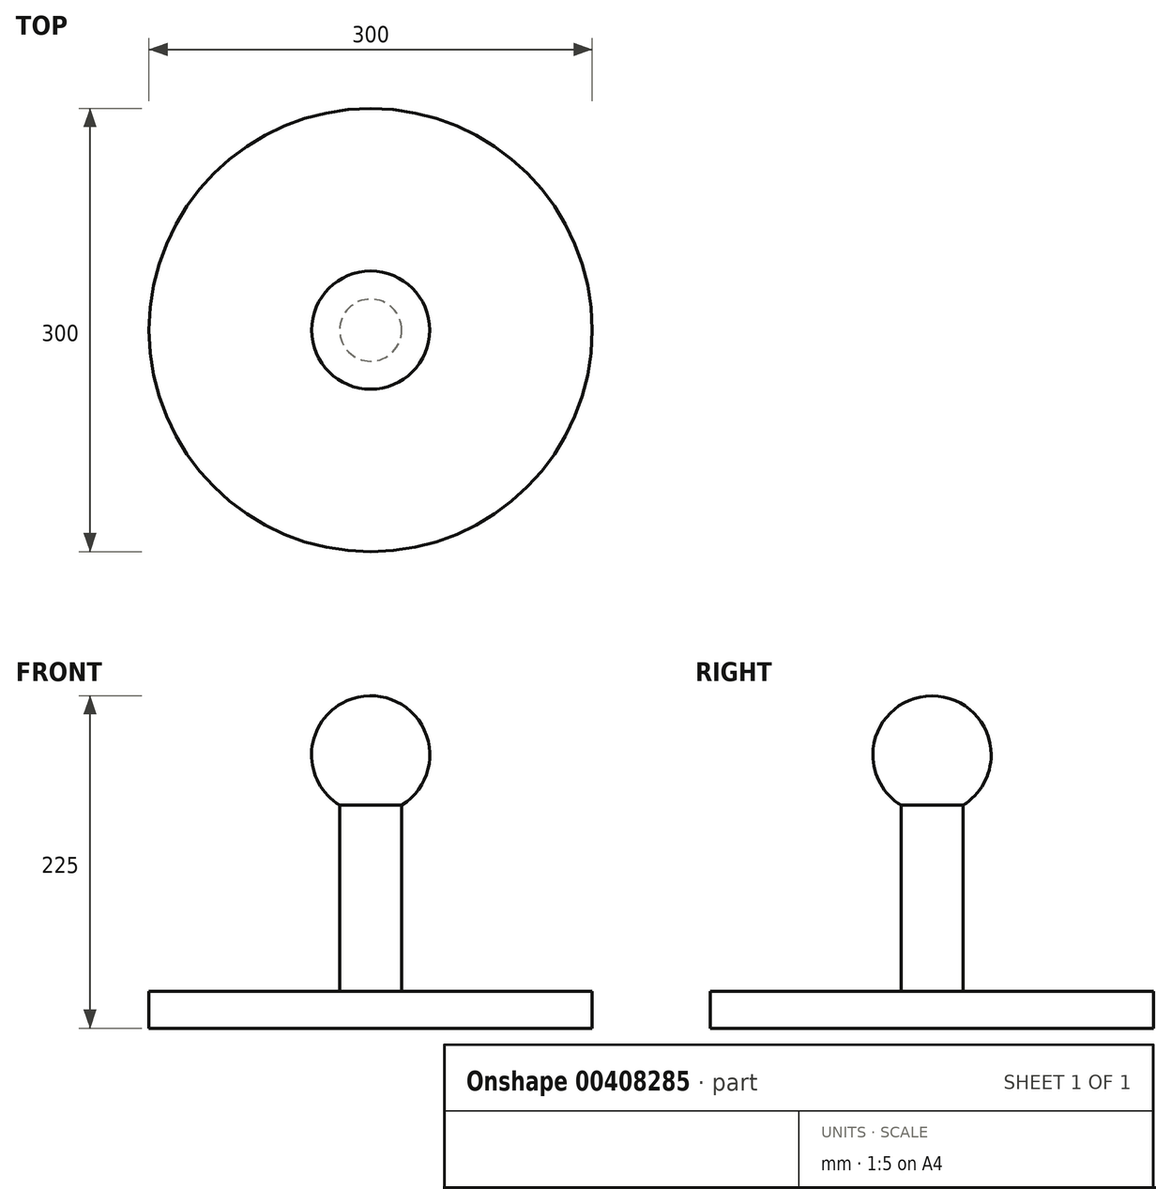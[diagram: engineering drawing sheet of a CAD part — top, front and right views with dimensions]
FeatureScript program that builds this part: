
annotation { "Feature Type Name" : "Feature", "Feature Type Description" : "" }
export const myFeature = defineFeature(function(context is Context, id is Id, definition is map)
    precondition{}
    {
        {
            var Q0;
            Q0=qCreatedBy(makeId("Top.planeOp"),FACE);
            var sketch = newSketch(context, id + "F0", { "sketchPlane" : qUnion([Q0])});
            skCircle(sketch, "E0", {"center": v(0, 0) * mm, "radius": 150 * mm});
            skSolve(sketch);
        }
        {
            var Q0;
            Q0=makeQuery(id+"F0.imprint","IMPRINT",FACE,{"disambiguationData":[TD([[makeQuery(id+"F0.imprint","IMPRINT",EDGE,{"derivedFrom":sQuery(id+"F0.wireOp",EDGE,"E0")}),1.0]])]});
            extrude(context, id + "F1", {"entities" : qUnion([Q0]), "depth" : 25 * mm});
        }
        {
            var Q0;
            Q0=makeQuery(id+"F1.opExtrude","CAP_FACE",FACE,{"disambiguationData":[OSD([sQuery(id+"F0.wireOp",EDGE,"E0")])],"isStart":false});
            var sketch = newSketch(context, id + "F2", { "sketchPlane" : qUnion([Q0])});
            skCircle(sketch, "E1", {"center": v(0, 0) * mm, "radius": 21 * mm});
            skSolve(sketch);
        }
        {
            var Q0;
            Q0=makeQuery(id+"F2.imprint","IMPRINT",FACE,{"disambiguationData":[TD([[makeQuery(id+"F2.imprint","IMPRINT",EDGE,{"derivedFrom":sQuery(id+"F2.wireOp",EDGE,"E1")}),1.0]])]});
            extrude(context, id + "F3", {"entities" : qUnion([Q0]), "operationType" : NewBodyOperationType.ADD, "depth" : 160 * mm});
        }
        {
            var Q0;
            Q0=makeQuery(id+"F3.opExtrude","CAP_FACE",FACE,{"disambiguationData":[OSD([sQuery(id+"F2.wireOp",EDGE,"E1")])],"isStart":false});
            var sketch = newSketch(context, id + "F4", { "sketchPlane" : qUnion([Q0])});
            skArc(sketch, "E2", {"start": v(0, 40) * mm, "mid": v(-40, 0) * mm, "end": v(0, -40) * mm});
            skLineSegment(sketch, "E3", {"start": v(0, -40) * mm, "end": v(0, 40) * mm});
            skSolve(sketch);
        }
        {
            var Q0;
            {var subQ0=sQuery(id+"F4.wireOp",EDGE,"E2");Q0=makeQuery(id+"F4.imprint","IMPRINT",FACE,{"disambiguationData":[TD([[makeQuery(id+"F4.imprint","IMPRINT",EDGE,{"derivedFrom":subQ0}),1.0]])]});}
            var Q1;
            {var subQ0=sQuery(id+"F4.wireOp",EDGE,"E3");var subQ1=makeQuery(id+"F3.opExtrude","CAP_EDGE",EDGE,{"disambiguationData":[OSD([sQuery(id+"F2.wireOp",EDGE,"E1")])],"isStart":false});var subQ2=makeQuery(id+"F4.imprint","INTERSECT",VERTEX,{"disambiguationData":[OD(0.0)],"derivedFrom":[subQ1,subQ0]});Q1=makeQuery(id+"F4.imprint","IMPRINT",FACE,{"disambiguationData":[TD([[makeQuery(id+"F4.imprint","IMPRINT",EDGE,{"disambiguationData":[TD([[subQ2,-1.0]])],"derivedFrom":subQ0}),1.0]])]});}
            var Q2;
            Q2=sQuery(id+"F4.wireOp",EDGE,"E3");
            revolve(context, id + "F5", {"operationType" : NewBodyOperationType.ADD, "entities" : qUnion([Q0, Q1]), "axis" : qUnion([Q2]), "revolveType" : RevolveType.FULL});
        }
    });
